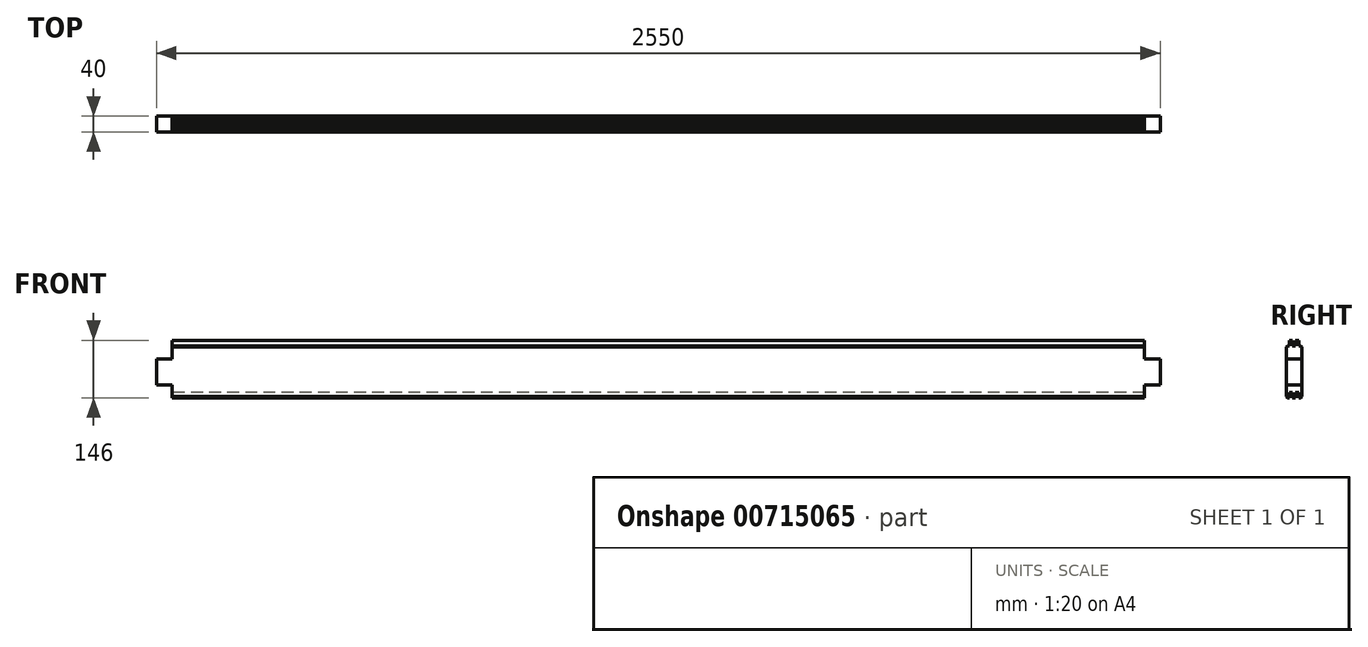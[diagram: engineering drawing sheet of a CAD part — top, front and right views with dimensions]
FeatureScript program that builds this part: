
annotation { "Feature Type Name" : "Feature", "Feature Type Description" : "" }
export const myFeature = defineFeature(function(context is Context, id is Id, definition is map)
    precondition{}
    {
        {
            assignVariable(context, id + "F0", {"name" : "Laenge", "anyValue" : 2550});
        }
        {
            var Q0;
            Q0=qCreatedBy(makeId("Right.planeOp"),FACE);
            var sketch = newSketch(context, id + "F1", { "sketchPlane" : qUnion([Q0])});
            skLineSegment(sketch, "E0", {"start": v(20, 63) * mm, "end": v(20, -63) * mm});
            skLineSegment(sketch, "E1", {"start": v(20, -63) * mm, "end": v(17, -66) * mm});
            skLineSegment(sketch, "E2", {"start": v(17, -66) * mm, "end": v(12, -66) * mm});
            skLineSegment(sketch, "E3", {"start": v(12, -52) * mm, "end": v(12, -66) * mm});
            skLineSegment(sketch, "E4", {"start": v(12, -52) * mm, "end": v(4, -52) * mm});
            skLineSegment(sketch, "E5", {"start": v(4, -66) * mm, "end": v(4, -52) * mm});
            skLineSegment(sketch, "E6", {"start": v(4, -66) * mm, "end": v(-4, -66) * mm});
            skLineSegment(sketch, "E7", {"start": v(-4, -52) * mm, "end": v(-4, -66) * mm});
            skLineSegment(sketch, "E8", {"start": v(-4, -52) * mm, "end": v(-12, -52) * mm});
            skLineSegment(sketch, "E9", {"start": v(-12, -66) * mm, "end": v(-12, -52) * mm});
            skLineSegment(sketch, "E10", {"start": v(-12, -66) * mm, "end": v(-17, -66) * mm});
            skLineSegment(sketch, "E11", {"start": v(-17, -66) * mm, "end": v(-20, -63) * mm});
            skLineSegment(sketch, "E12", {"start": v(-20, -63) * mm, "end": v(-20, 63) * mm});
            skLineSegment(sketch, "E13", {"start": v(-20, 63) * mm, "end": v(-17, 66) * mm});
            skLineSegment(sketch, "E14", {"start": v(-17, 66) * mm, "end": v(-12, 66) * mm});
            skLineSegment(sketch, "E15", {"start": v(-4, 66) * mm, "end": v(4, 66) * mm});
            skLineSegment(sketch, "E16", {"start": v(12, 66) * mm, "end": v(17, 66) * mm});
            skLineSegment(sketch, "E17", {"start": v(17, 66) * mm, "end": v(20, 63) * mm});
            skPoint(sketch, "E18.end.orphan", {"position": v(12, 57.8) * mm});
            skPoint(sketch, "E19.end.orphan", {"position": v(4, 66.3) * mm});
            skPoint(sketch, "E20.end.orphan", {"position": v(-4, 66.3) * mm});
            skLineSegment(sketch, "E21", {"start": v(-12, 66) * mm, "end": v(-12, 80) * mm});
            skLineSegment(sketch, "E22", {"start": v(-12, 80) * mm, "end": v(-4, 80) * mm});
            skLineSegment(sketch, "E23", {"start": v(-4, 80) * mm, "end": v(-4, 66) * mm});
            skLineSegment(sketch, "E24", {"start": v(4, 66) * mm, "end": v(4, 80) * mm});
            skLineSegment(sketch, "E25", {"start": v(4, 80) * mm, "end": v(12, 80) * mm});
            skLineSegment(sketch, "E26", {"start": v(12, 80) * mm, "end": v(12, 66) * mm});
            skLineSegment(sketch, "E27", {"start": v(20, -33) * mm, "end": v(-20, -33) * mm});
            skLineSegment(sketch, "E28", {"start": v(20, 33) * mm, "end": v(-20, 33) * mm});
            skPoint(sketch, "E29.end.orphan", {"position": v(-141.42, 0) * mm});
            skLineSegment(sketch, "E30", {"start": v(20, 0) * mm, "end": v(-20, 0) * mm});
            skLineSegment(sketch, "E31", {"start": v(20, 0) * mm, "end": v(-20, 0) * mm, "construction": true});
            skLineSegment(sketch, "E32", {"start": v(0, 33) * mm, "end": v(0, -33) * mm, "construction": true});
            skSolve(sketch);
        }
        {
            var Q0;
            Q0=qCreatedBy(makeId("Front.planeOp"),FACE);
            var sketch = newSketch(context, id + "F2", { "sketchPlane" : qUnion([Q0])});
            skLineSegment(sketch, "E33", {"start": v(1275, 0) * mm, "end": v(-1275, 0) * mm, "construction": true});
            skPoint(sketch, "E34.right.start.orphan", {"position": v(-259.12, 108.1) * mm});
            skPoint(sketch, "E35.left.start.orphan", {"position": v(237.35, 108.1) * mm});
            skPoint(sketch, "E36.left.end.orphan", {"position": v(237.35, -84.05) * mm});
            skPoint(sketch, "E36.bottom.start.orphan", {"position": v(237.35, -117.05) * mm});
            skPoint(sketch, "E37.right.start.orphan", {"position": v(-259.12, -117.05) * mm});
            skPoint(sketch, "E37.top.end.orphan", {"position": v(-259.12, -84.05) * mm});
            skLineSegment(sketch, "E38.bottom", {"start": v(-1315, 33) * mm, "end": v(-1235, 33) * mm});
            skLineSegment(sketch, "E38.top", {"start": v(-1315, 133) * mm, "end": v(-1235, 133) * mm});
            skLineSegment(sketch, "E38.left", {"start": v(-1315, 33) * mm, "end": v(-1315, 133) * mm});
            skLineSegment(sketch, "E38.right", {"start": v(-1235, 33) * mm, "end": v(-1235, 133) * mm});
            skPoint(sketch, "E38.middle", {"position": v(-1275, 83) * mm});
            skLineSegment(sketch, "E39.bottom", {"start": v(-1315, -133) * mm, "end": v(-1235, -133) * mm});
            skLineSegment(sketch, "E39.top", {"start": v(-1315, -33) * mm, "end": v(-1235, -33) * mm});
            skLineSegment(sketch, "E39.left", {"start": v(-1315, -133) * mm, "end": v(-1315, -33) * mm});
            skLineSegment(sketch, "E39.right", {"start": v(-1235, -133) * mm, "end": v(-1235, -33) * mm});
            skPoint(sketch, "E39.middle", {"position": v(-1275, -83) * mm});
            skLineSegment(sketch, "E40.bottom", {"start": v(1315, 33) * mm, "end": v(1235, 33) * mm});
            skLineSegment(sketch, "E40.top", {"start": v(1315, 133) * mm, "end": v(1235, 133) * mm});
            skLineSegment(sketch, "E40.left", {"start": v(1315, 33) * mm, "end": v(1315, 133) * mm});
            skLineSegment(sketch, "E40.right", {"start": v(1235, 33) * mm, "end": v(1235, 133) * mm});
            skPoint(sketch, "E40.middle", {"position": v(1275, 83) * mm});
            skLineSegment(sketch, "E41.bottom", {"start": v(1315, -33) * mm, "end": v(1235, -33) * mm});
            skLineSegment(sketch, "E41.top", {"start": v(1315, -133) * mm, "end": v(1235, -133) * mm});
            skLineSegment(sketch, "E41.left", {"start": v(1315, -33) * mm, "end": v(1315, -133) * mm});
            skLineSegment(sketch, "E41.right", {"start": v(1235, -33) * mm, "end": v(1235, -133) * mm});
            skPoint(sketch, "E41.middle", {"position": v(1275, -83) * mm});
            skSolve(sketch);
        }
        {
            var Q0;
            {var subQ3=sQuery(id+"F1.wireOp",EDGE,"E13");Q0=makeQuery(id+"F1.imprint","IMPRINT",FACE,{"disambiguationData":[TD([[makeQuery(id+"F1.imprint","IMPRINT",EDGE,{"derivedFrom":subQ3}),-1.0]])]});}
            var Q1;
            {var subQ0=sQuery(id+"F1.wireOp",EDGE,"E28");Q1=makeQuery(id+"F1.imprint","IMPRINT",FACE,{"disambiguationData":[TD([[makeQuery(id+"F1.imprint","IMPRINT",EDGE,{"derivedFrom":subQ0}),1.0]])]});}
            var Q2;
            {var subQ0=sQuery(id+"F1.wireOp",EDGE,"E27");Q2=makeQuery(id+"F1.imprint","IMPRINT",FACE,{"disambiguationData":[TD([[makeQuery(id+"F1.imprint","IMPRINT",EDGE,{"derivedFrom":subQ0}),-1.0]])]});}
            var Q3;
            {var subQ1=sQuery(id+"F1.wireOp",EDGE,"E1");Q3=makeQuery(id+"F1.imprint","IMPRINT",FACE,{"disambiguationData":[TD([[makeQuery(id+"F1.imprint","IMPRINT",EDGE,{"derivedFrom":subQ1}),-1.0]])]});}
            extrude(context, id + "F3", {"entities" : qUnion([Q0, Q1, Q2, Q3]), "endBound" : BoundingType.SYMMETRIC, "depth" : getVariable(context, 'Laenge') * mm, "offsetDistance" : 25 * mm});
        }
        {
            var Q0;
            Q0=makeQuery(id+"F2.imprint","IMPRINT",FACE,{"disambiguationData":[TD([[makeQuery(id+"F2.imprint","IMPRINT",EDGE,{"derivedFrom":sQuery(id+"F2.wireOp",EDGE,"E38.bottom")}),1.0]])]});
            var Q1;
            Q1=makeQuery(id+"F2.imprint","IMPRINT",FACE,{"disambiguationData":[TD([[makeQuery(id+"F2.imprint","IMPRINT",EDGE,{"derivedFrom":sQuery(id+"F2.wireOp",EDGE,"E39.bottom")}),1.0]])]});
            var Q2;
            Q2=makeQuery(id+"F2.imprint","IMPRINT",FACE,{"disambiguationData":[TD([[makeQuery(id+"F2.imprint","IMPRINT",EDGE,{"derivedFrom":sQuery(id+"F2.wireOp",EDGE,"E40.bottom")}),-1.0]])]});
            var Q3;
            Q3=makeQuery(id+"F2.imprint","IMPRINT",FACE,{"disambiguationData":[TD([[makeQuery(id+"F2.imprint","IMPRINT",EDGE,{"derivedFrom":sQuery(id+"F2.wireOp",EDGE,"E41.bottom")}),1.0]])]});
            extrude(context, id + "F4", {"entities" : qUnion([Q0, Q1, Q2, Q3]), "operationType" : NewBodyOperationType.REMOVE, "endBound" : BoundingType.SYMMETRIC, "oppositeDirection" : true, "depth" : 50 * mm, "offsetDistance" : 25 * mm});
        }
    });
